# Revit family: Camera-Security-Panasonic-Super_Dynamic_FullHD-Weather_Resistant-PTZ-Dome-Network-SW598ASeries
name_source: partatom
category: Security Devices
revit_build: Autodesk Revit 2013 (Build: 20130531_2115(x64)
units: mm (PartAtom-declared; Revit-internal decimal feet)

## types (1)
- Standard, SW598A
    Alarm Input Or Output Specification = ALARM IN 1 (DAY/NIGHT IN), ALARM IN 2 (ALARM OUT), ALARM IN 3 (AUX OUT)
    Angle Of View = 63
    Audio In = Yes
    Audio Out = Yes
    Communication Ports = 10Base-T / 100Base-TX, RJ45 connector
    Date Last Modified = Feb 17, 2017
    Day Or Night = Yes
    Default Elevation = 0 "
    Description = Security Camera, Super Dynamic Full HD, Weather Resistant, PTZ, Dome, Network, SW598A
    Diameter = 9.016 "
    Equipment Abbreviation = SC
    Family Version = 1.0.0
    HFOV Max 169 = 63.00°
    HFOV Max 43 = 46.00°
    HFOV Min 169 = 2.60°
    HFOV Min 43 = 1.90°
    Has POE = Yes
    Height = 15.433 "
    IP Or Analog = IP
    Indoor Or Outdoor = Outdoor
    Manufacturer = Panasonic
    Minimum Illumination = 0 lx
    Model = WV-SW598A
    Model Disclaimer = Contact Panasonic for more information
    Mounting Positions = Mount Dependent
    Operational Humidity = 10 % to 90 % (no condensation)
    Operational Temperature = -58°F - 131°F
    Pan Max = 360.00°
    Pan Min = 0.00°
    Panning Range = 360
    Part Description = Security Camera, Super Dynamic Full HD, Weather Resistant, PTZ, Dome, Network, SW598A
    Part Number = WV-SW598A
    Power Active = 55.0 W
    Product Documentation Link = http://ssbu-t.psn-web.net
    Product Material = Paint - Panasonic - Silver
    Product Page URL = http://security.panasonic.com
    Provide Feedback = https://www.surveymonkey.com
    Regulatory Compliance = UL60950-1, C-UL CAN/CSA C22.2 No.60950-1, CE, IEC60950-1,FCC Part15 Class A, ICES-003 Class A, EN55022 Class B, EN55024
    Shock resistance = Yes
    Storage Temperature = -58°F - 131°F
    Tilt Max = 195.00°
    Tilt Min = -15.00°
    Tilting Range = -15 to +195
    URL = http://security.panasonic.com
    VFOV Max 169 = 37.00°
    VFOV Max 43 = 37.00°
    VFOV Min 169 = 1.50°
    VFOV Min 43 = 1.50°
    Vandal Resistant = Yes
    Voltage AC = 24 V
    Water and Dust Resistance = Yes
    Weight = 11.02 lb
    Wide Dynamic Range = Yes
    z Camera Resolution Type = 0
    z Const Pan Handle Length = 27.559 "
    z Const Tilt Base Length = 14.173 "
    z Const Tilt Base2 Length = 19.685 "
    z Const Tilt Handle Length = 14.173 "
    z Const Yaw Base Length = 9.843 "
    z Const Yaw Base2 Length = 500.00°
    z Const Yaw Handle Length = 9.252 "
    z VV Viewpoint Depth Max = 2.143 "
    z VV Viewpoint Depth Min = 2.143 "

## geometry (parser evidence)
native form markers: Sweep x10
no freeform markers — native parametric forms only
